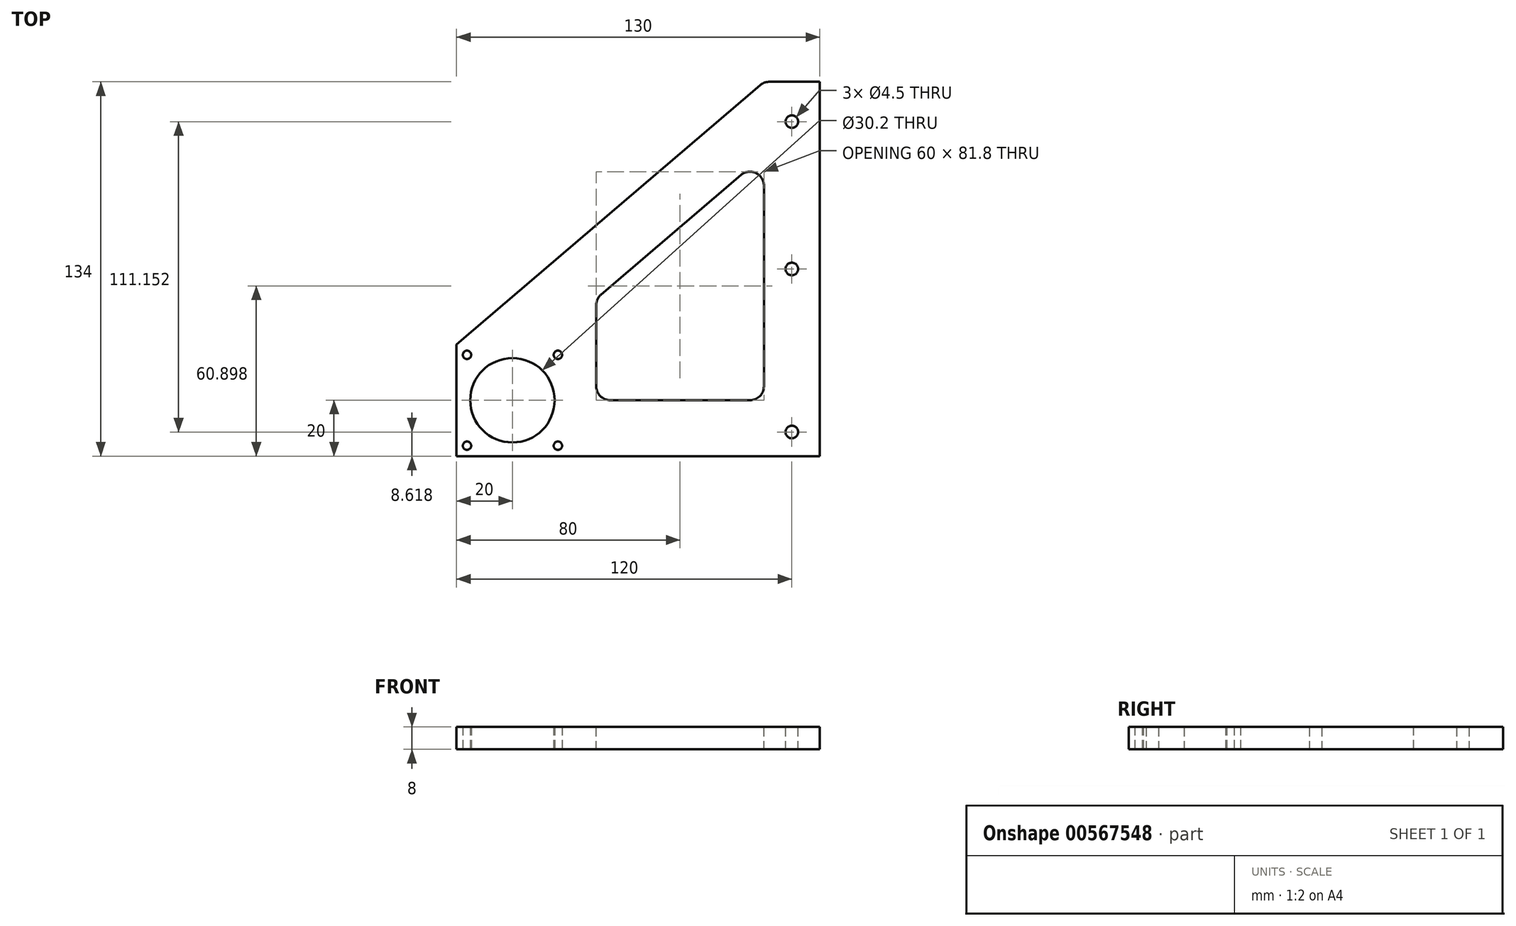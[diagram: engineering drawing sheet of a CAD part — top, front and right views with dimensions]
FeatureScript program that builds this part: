
annotation { "Feature Type Name" : "Feature", "Feature Type Description" : "" }
export const myFeature = defineFeature(function(context is Context, id is Id, definition is map)
    precondition{}
    {
        {
            var Q0;
            Q0=qCreatedBy(makeId("Top.planeOp"),FACE);
            var sketch = newSketch(context, id + "F0", { "sketchPlane" : qUnion([Q0])});
            skLineSegment(sketch, "E0.bottom", {"start": v(65, -20) * mm, "end": v(-65, -20) * mm});
            skLineSegment(sketch, "E0.top", {"start": v(65, 20) * mm, "end": v(-65, 20) * mm});
            skLineSegment(sketch, "E0.left", {"start": v(65, -20) * mm, "end": v(65, 20) * mm});
            skLineSegment(sketch, "E0.right", {"start": v(-65, -20) * mm, "end": v(-65, 20) * mm});
            skPoint(sketch, "E0.middle", {"position": v(0, 0) * mm});
            skCircle(sketch, "E1", {"center": v(-45, 0) * mm, "radius": 23 * mm, "construction": true});
            skLineSegment(sketch, "E2.bottom", {"start": v(-28.74, 16.26) * mm, "end": v(-61.26, 16.26) * mm, "construction": true});
            skLineSegment(sketch, "E2.top", {"start": v(-28.74, -16.26) * mm, "end": v(-61.26, -16.26) * mm, "construction": true});
            skLineSegment(sketch, "E2.left", {"start": v(-28.74, 16.26) * mm, "end": v(-28.74, -16.26) * mm, "construction": true});
            skLineSegment(sketch, "E2.right", {"start": v(-61.26, 16.26) * mm, "end": v(-61.26, -16.26) * mm, "construction": true});
            skCircle(sketch, "E3", {"center": v(-61.26, 16.26) * mm, "radius": 1.5 * mm});
            skCircle(sketch, "E4", {"center": v(-28.74, 16.26) * mm, "radius": 1.5 * mm});
            skCircle(sketch, "E5", {"center": v(-28.74, -16.26) * mm, "radius": 1.5 * mm});
            skCircle(sketch, "E6", {"center": v(-61.26, -16.26) * mm, "radius": 1.5 * mm});
            skCircle(sketch, "E7", {"center": v(-45, 0) * mm, "radius": 15.1 * mm});
            skSolve(sketch);
        }
        {
            var Q0;
            Q0 = qSketchRegion(id + "F0", true);
            extrude(context, id + "F1", {"entities" : qUnion([Q0]), "depth" : 8 * mm, "offsetDistance" : 25 * mm});
        }
        {
            var Q0;
            Q0=makeQuery(id+"F1.opExtrude","CAP_FACE",FACE,{"disambiguationData":[OSD([sQuery(id+"F0.wireOp",EDGE,"E0.bottom"),sQuery(id+"F0.wireOp",EDGE,"E0.top"),sQuery(id+"F0.wireOp",EDGE,"E0.left"),sQuery(id+"F0.wireOp",EDGE,"E0.right"),sQuery(id+"F0.wireOp",EDGE,"E3"),sQuery(id+"F0.wireOp",EDGE,"E4"),sQuery(id+"F0.wireOp",EDGE,"E5"),sQuery(id+"F0.wireOp",EDGE,"E6"),sQuery(id+"F0.wireOp",EDGE,"E7")])],"isStart":false});
            var sketch = newSketch(context, id + "F2", { "sketchPlane" : qUnion([Q0])});
            skLineSegment(sketch, "E8", {"start": v(65, 114) * mm, "end": v(65, 20) * mm});
            skLineSegment(sketch, "E9", {"start": v(65, 20) * mm, "end": v(-65, 20) * mm});
            skLineSegment(sketch, "E10", {"start": v(-65, 20) * mm, "end": v(45, 114) * mm});
            skLineSegment(sketch, "E11", {"start": v(45, 114) * mm, "end": v(65, 114) * mm});
            skSolve(sketch);
        }
        {
            var Q0;
            Q0=makeQuery(id+"F2.imprint","IMPRINT",FACE,{"disambiguationData":[TD([[makeQuery(id+"F2.imprint","IMPRINT",EDGE,{"derivedFrom":sQuery(id+"F2.wireOp",EDGE,"E8")}),-1.0]])]});
            extrude(context, id + "F3", {"entities" : qUnion([Q0]), "operationType" : NewBodyOperationType.ADD, "oppositeDirection" : true, "depth" : 8 * mm, "offsetDistance" : 25 * mm});
        }
        {
            var Q0;
            Q0=makeQuery(id+"F3.boolean.opBoolean","MERGE",FACE,{"derivedFrom":[makeQuery(id+"F1.opExtrude","CAP_FACE",FACE,{"disambiguationData":[OSD([sQuery(id+"F0.wireOp",EDGE,"E0.bottom"),sQuery(id+"F0.wireOp",EDGE,"E0.top"),sQuery(id+"F0.wireOp",EDGE,"E0.left"),sQuery(id+"F0.wireOp",EDGE,"E0.right"),sQuery(id+"F0.wireOp",EDGE,"E3"),sQuery(id+"F0.wireOp",EDGE,"E4"),sQuery(id+"F0.wireOp",EDGE,"E5"),sQuery(id+"F0.wireOp",EDGE,"E6"),sQuery(id+"F0.wireOp",EDGE,"E7")])],"isStart":false}),makeQuery(id+"F3.opExtrude","CAP_FACE",FACE,{"disambiguationData":[OSD([sQuery(id+"F2.wireOp",EDGE,"E8"),sQuery(id+"F2.wireOp",EDGE,"E9"),sQuery(id+"F2.wireOp",EDGE,"E10"),sQuery(id+"F2.wireOp",EDGE,"E11")])],"isStart":true})]});
            var sketch = newSketch(context, id + "F4", { "sketchPlane" : qUnion([Q0])});
            skLineSegment(sketch, "E12", {"start": v(-15, 0) * mm, "end": v(-15, 36.42) * mm});
            skLineSegment(sketch, "E13", {"start": v(-15, 36.42) * mm, "end": v(45, 87.7) * mm});
            skLineSegment(sketch, "E14", {"start": v(45, 87.7) * mm, "end": v(45, 0) * mm});
            skLineSegment(sketch, "E15", {"start": v(45, 0) * mm, "end": v(-15, 0) * mm});
            skCircle(sketch, "E16", {"center": v(55, 99.77) * mm, "radius": 2.25 * mm});
            skCircle(sketch, "E17", {"center": v(55, 47) * mm, "radius": 2.25 * mm});
            skCircle(sketch, "E18", {"center": v(55, -11.38) * mm, "radius": 2.25 * mm});
            skSolve(sketch);
        }
        {
            var Q0;
            Q0 = qSketchRegion(id + "F4", true);
            extrude(context, id + "F5", {"entities" : qUnion([Q0]), "operationType" : NewBodyOperationType.REMOVE, "endBound" : BoundingType.THROUGH_ALL, "oppositeDirection" : true, "depth" : 25 * mm, "offsetDistance" : 25 * mm});
        }
        {
            var Q0;
            Q0=makeQuery(id+"F3.opExtrude","SWEPT_EDGE",EDGE,{"disambiguationData":[OSD([sQuery(id+"F2.wireOp",EDGE,"E10"),sQuery(id+"F2.wireOp",EDGE,"E11")])]});
            var Q1;
            Q1=makeQuery(id+"F5.boolean.opBoolean","COPY",EDGE,{"derivedFrom":makeQuery(id+"F5.opExtrude","SWEPT_EDGE",EDGE,{"disambiguationData":[OSD([sQuery(id+"F4.wireOp",EDGE,"E12"),sQuery(id+"F4.wireOp",EDGE,"E13")])]})});
            var Q2;
            Q2=makeQuery(id+"F5.boolean.opBoolean","COPY",EDGE,{"derivedFrom":makeQuery(id+"F5.opExtrude","SWEPT_EDGE",EDGE,{"disambiguationData":[OSD([sQuery(id+"F4.wireOp",EDGE,"E13"),sQuery(id+"F4.wireOp",EDGE,"E14")])]})});
            var Q3;
            Q3=makeQuery(id+"F5.boolean.opBoolean","COPY",EDGE,{"derivedFrom":makeQuery(id+"F5.opExtrude","SWEPT_EDGE",EDGE,{"disambiguationData":[OSD([sQuery(id+"F4.wireOp",EDGE,"E14"),sQuery(id+"F4.wireOp",EDGE,"E15")])]})});
            var Q4;
            Q4=makeQuery(id+"F5.boolean.opBoolean","COPY",EDGE,{"derivedFrom":makeQuery(id+"F5.opExtrude","SWEPT_EDGE",EDGE,{"disambiguationData":[OSD([sQuery(id+"F4.wireOp",EDGE,"E12"),sQuery(id+"F4.wireOp",EDGE,"E15")])]})});
            fillet(context, id + "F6", {"entities" : qUnion([Q0, Q1, Q2, Q3, Q4]), "radius" : 5 * mm, "tangentPropagation" : true, "allowEdgeOverflow" : false});
        }
    });
